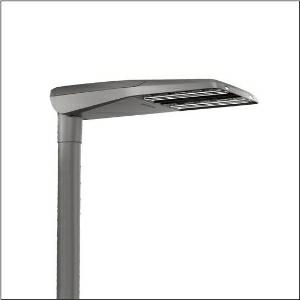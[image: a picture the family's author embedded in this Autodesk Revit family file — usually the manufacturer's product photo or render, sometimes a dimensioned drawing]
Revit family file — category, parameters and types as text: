
# Revit family: streetlight_sl_11_iq_midi___st1_2p1_0_5xc3g41f08me_0c33
name_source: partatom
category: Lighting Fixtures
units: mm (PartAtom-declared; Revit-internal decimal feet)

## family parameters
Cut with Voids When Loaded = No
Host = Face
Light Source = No
Part Type = Normal
Room Calculation Point = No
Round Connector Dimension = Use Diameter
Shared = No

## types (1)
- --- (1 x LED, 18520 lm, 121.7 W, 4000K)
    Apparent Load = 122 VA
    CIE Flux Codes = 31 68 95 100 100
    Color Rendering = 70
    Color Temperature = 4000K
    Default Elevation = 1800 mm
    Description = Streetlight SL 11 iQ midi, mast luminaire, primary light control with 3 zone facetted reflector, of plastic, silver coated, highly specular, primary optical cover: cover, of PMMA, transparent, light distribution: ST1.2P1.0, light emission: direct distribution, primary light characteristic: asymmetric, installation type: post-top, side-entry, lamps: LED, High Power LED, rated values: 18.520lm | 121,7W | 152,2lm/W (begin service life); end service life: 18.520lm | 129W; at 50% lumin. flux: 9.260lm | 56,2W | 164,8lm/W, colour temperature: 4000K, colour rendering: CRI > 70, light colour: 740, light setting 1 begin service life: 100% | 18.520lm | 121,7W | 152,2lm/W | 4.000K, light setting 1 end service life: 129W, further light settings possible, control: Street-Remote, optimised constant luminous flux control (CLO 2.0), Auto-Match, Desk-Remote (wireless, voltage-free reading and setting of iQ features in the workshop via application-optimized NFC function/RFID function), Light-Fading, Smart-Wire, Night-Set, Lumen-Switch, Temp-Guard, with cable H07RN-F 3x 1.5mm², mains connection: 230..240V, AC, 50/60Hz, connection cable pre-assembled, cable length: 12,5m, luminaire housing, of diecast aluminium, powder-coated, SITECO metallic grey (DB 702S), please order mast flange separately, inclination adjustable without tools: 0°, 5°, 10°, 15° (post-top) | 0°, -5°, -10°, -15° (side-entry), sealing non-destructively replaceable, multi-level sealing system, length: 780mm, width: 376mm, height: 118mm, mast flange for spigot size: 42mm (side-entry): 5XC10008XM4, 60/48mm (side-entry/post-top): 5XC10108XM2, 76/60mm (side-entry/post-top): 5XC10108XM1, equipment: Power, protection rating (complete): IP66, insulation class (complete): insulation class II (safety insulation), certification: CE, ENEC, ENEC+, VDE, impact resistance: IK10, permissible operating ambient temperature for outdoor applications: -25..+50°C, standard-compliant lighting for roads and squares, Environmental Product Declaration (EPD) tested and certified by an independent institute, packaging unit: 1 piece

Light Distribution: ST1.2P1.0
    Height = 118 mm
    Lamp = 1 x LED
    Lamp Light Flux = 18520 lm
    Lamp Power = 121.7 W
    Lamp count = 1
    Length = 780 mm
    Luminous efficacy = 152 lm/W
    Manufacturer = Siteco
    ModVariant = No
    Model = 5XC3G41F08ME
    Number of Poles = 1
    OnlyDefault = Yes
    Power Factor = 1
    Product Name = Streetlight SL 11 iQ midi | ST1.2P1.0
    Product group = mast luminaire | pylon top
    ProductGroupID = 6100
    Protection Class = Protection class II
    Protection Degree = IP 66
    RLX_Detail_Level = 1
    RLX_Emergency_Light_Flux = 0 lm
    RLX_Emergency_Type = 0
    RLX_Emergency_Type_DB = No
    RlxData = <blob elided: 70893 chars, md5=638c0baa>
    Socket = socket
    Standby Power = 0 W
    System Light Flux = 18520 lm
    System Power = 122 W
    Type Comments = factory setting: luminous flux: 100 % | dim-lin: 254 | 544 mA
    Type Image = l_1005960.jpg
    URL = http://relux.com
    VarID = @adj_044207
    Voltage = 0 V
    Weight = 0.00 kg
    Width = 376 mm

## geometry (parser evidence)
native form markers: Blend x4, Sweep x11
no freeform markers — native parametric forms only
